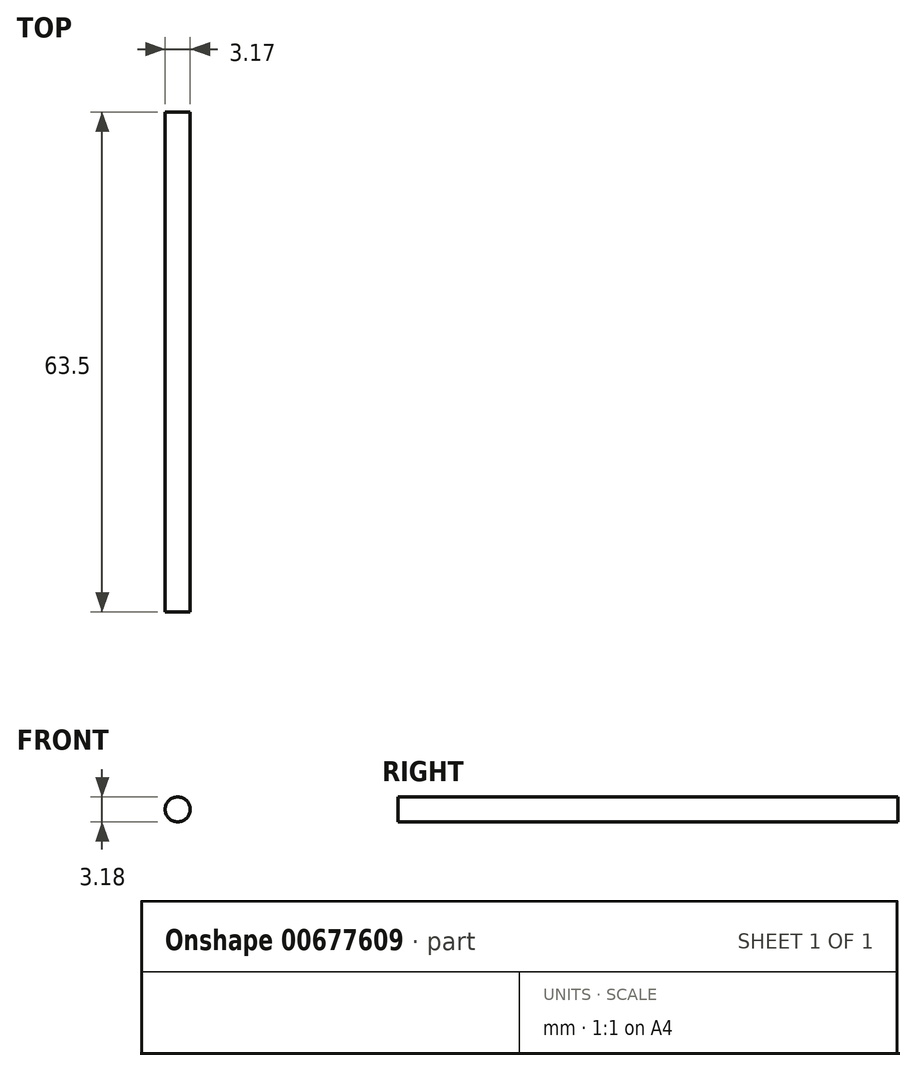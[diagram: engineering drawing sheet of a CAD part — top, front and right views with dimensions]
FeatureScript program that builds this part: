
annotation { "Feature Type Name" : "Feature", "Feature Type Description" : "" }
export const myFeature = defineFeature(function(context is Context, id is Id, definition is map)
    precondition{}
    {
        {
            var Q0;
            Q0=qCreatedBy(makeId("Front.planeOp"),FACE);
            var sketch = newSketch(context, id + "F0", { "sketchPlane" : qUnion([Q0])});
            skCircle(sketch, "E0", {"center": v(17.15, -22.48) * mm, "radius": 1.59 * mm});
            skSolve(sketch);
        }
        {
            var Q0;
            Q0 = qSketchRegion(id + "F0", true);
            extrude(context, id + "F1", {"entities" : qUnion([Q0]), "oppositeDirection" : true, "depth" : 63.5 * mm, "offsetDistance" : 25.4 * mm});
        }
    });
